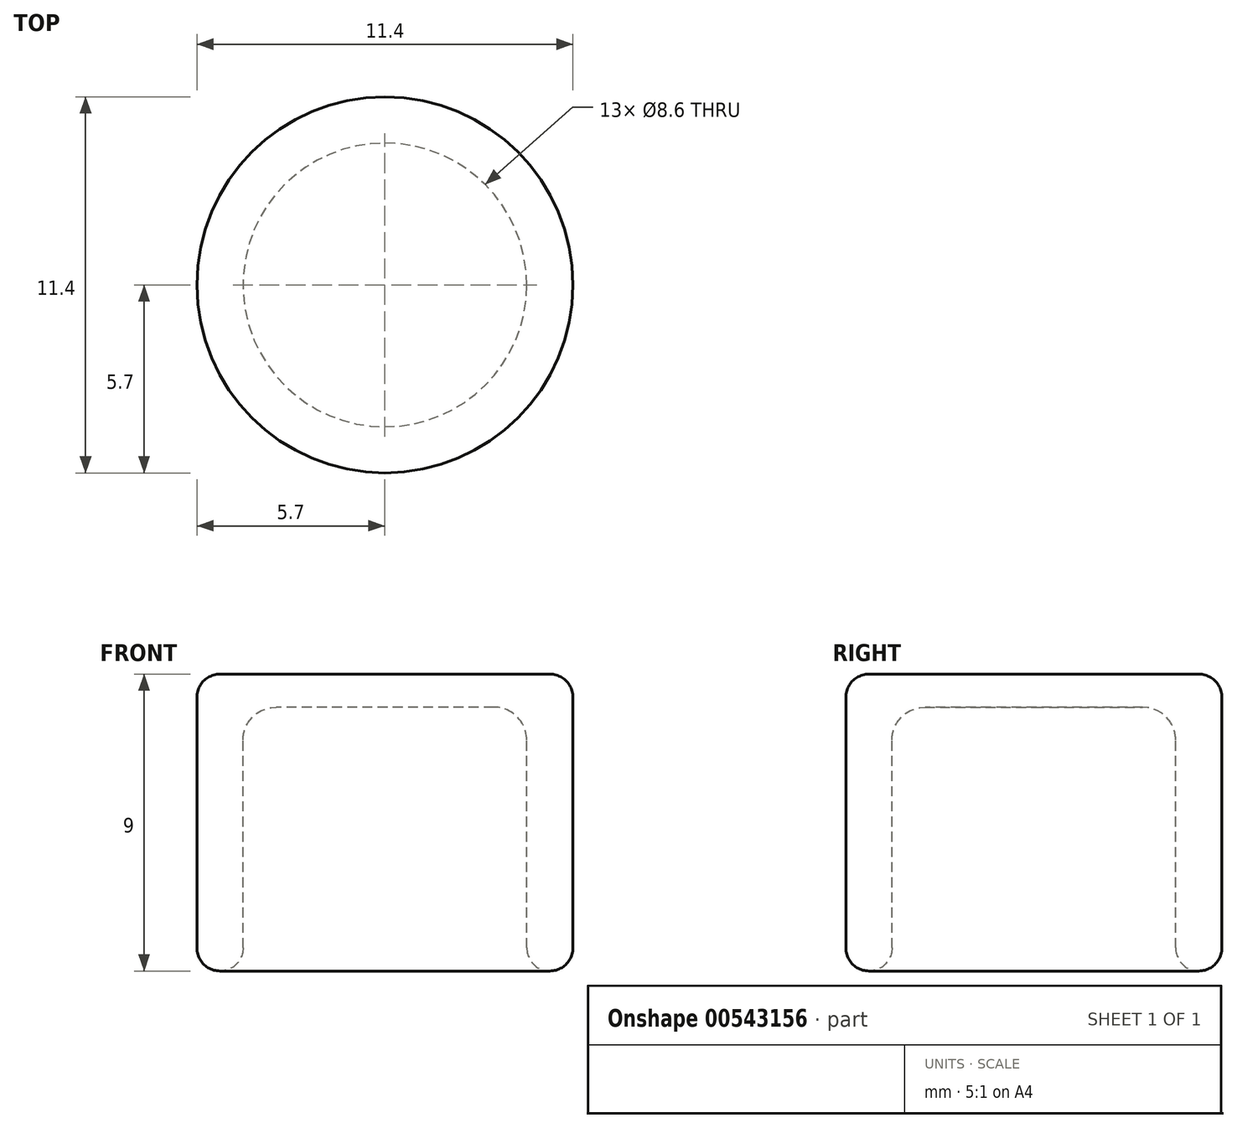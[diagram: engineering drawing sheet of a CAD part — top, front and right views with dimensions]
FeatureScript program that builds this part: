
annotation { "Feature Type Name" : "Feature", "Feature Type Description" : "" }
export const myFeature = defineFeature(function(context is Context, id is Id, definition is map)
    precondition{}
    {
        {
            var Q0;
            Q0=qCreatedBy(makeId("Front.planeOp"),FACE);
            var sketch = newSketch(context, id + "F0", { "sketchPlane" : qUnion([Q0])});
            skLineSegment(sketch, "E0", {"start": v(0, 8) * mm, "end": v(4.3, 8) * mm});
            skLineSegment(sketch, "E1", {"start": v(4.3, 8) * mm, "end": v(4.3, 0) * mm});
            skLineSegment(sketch, "E2", {"start": v(4.3, 0) * mm, "end": v(5.7, 0) * mm});
            skLineSegment(sketch, "E3", {"start": v(5.7, 0) * mm, "end": v(5.7, 9) * mm});
            skLineSegment(sketch, "E4", {"start": v(5.7, 9) * mm, "end": v(0, 9) * mm});
            skLineSegment(sketch, "E5", {"start": v(0, 9) * mm, "end": v(0, 8) * mm});
            skSolve(sketch);
        }
        {
            var Q0;
            Q0=makeQuery(id+"F0.imprint","IMPRINT",FACE,{"disambiguationData":[TD([[makeQuery(id+"F0.imprint","IMPRINT",EDGE,{"derivedFrom":sQuery(id+"F0.wireOp",EDGE,"E0")}),1.0]])]});
            var Q1;
            Q1=sQuery(id+"F0.wireOp",EDGE,"E5");
            revolve(context, id + "F1", {"entities" : qUnion([Q0]), "axis" : qUnion([Q1]), "revolveType" : RevolveType.FULL});
        }
        {
            var Q0;
            Q0=makeQuery(id+"F1.opRevolve","SWEPT_EDGE",EDGE,{"disambiguationData":[OSD([sQuery(id+"F0.wireOp",EDGE,"E2"),sQuery(id+"F0.wireOp",EDGE,"E3")])]});
            var Q1;
            Q1=makeQuery(id+"F1.opRevolve","SWEPT_EDGE",EDGE,{"disambiguationData":[OSD([sQuery(id+"F0.wireOp",EDGE,"E1"),sQuery(id+"F0.wireOp",EDGE,"E2")])]});
            var Q2;
            Q2=makeQuery(id+"F1.opRevolve","SWEPT_EDGE",EDGE,{"disambiguationData":[OSD([sQuery(id+"F0.wireOp",EDGE,"E3"),sQuery(id+"F0.wireOp",EDGE,"E4")])]});
            fillet(context, id + "F2", {"entities" : qUnion([Q0, Q1, Q2]), "radius" : 0.7 * mm, "tangentPropagation" : true, "allowEdgeOverflow" : false});
        }
        {
            var Q0;
            Q0=makeQuery(id+"F1.opRevolve","SWEPT_EDGE",EDGE,{"disambiguationData":[OSD([sQuery(id+"F0.wireOp",EDGE,"E0"),sQuery(id+"F0.wireOp",EDGE,"E1")])]});
            fillet(context, id + "F3", {"entities" : qUnion([Q0]), "radius" : 1 * mm, "tangentPropagation" : true, "allowEdgeOverflow" : false});
        }
    });
